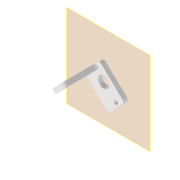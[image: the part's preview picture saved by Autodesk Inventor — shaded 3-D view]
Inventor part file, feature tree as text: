
AUTODESK INVENTOR PART (.ipt)
format: ipt  version: 2022 (Build 260153000, 153)  size: 141,824 bytes
history: native  units: mm
features: reference x11, extrude x3, sketch x3, other x3, plane x2, fillet x1, projected_geometry x1
ambient origin geometry x8: Origin, YZ Plane, XZ Plane, XY Plane, X Axis, Y Axis, Z Axis, Center Point
bodies: Body1 (feature_tree)
feature tree (24):
  plane  "Arbeitsebene3"
  extrude  "Extrusion4"  Depth=16.0mm
  sketch  "Skizze5"  dims[d17=24.0mm d18=3.0mm d19=0.0mm]
  plane  "Arbeitsebene4"
  extrude  "Extrusion5"  Depth=3.0mm TaperAngle=0.0deg
  extrude  "Extrusion6"  Depth=3.0mm TaperAngle=0.0deg
  fillet  "Rundung1"  Radius=10.0mm
  sketch  "Skizze4"  dims[d15=0.0mm d16=16.0mm]
  reference  "Referenz7"
  reference  "Referenz8"
  reference  "Referenz9"
  reference  "Referenz10"
  reference  "Referenz11"
  reference  "Referenz12"
  reference  "Referenz13"
  reference  "Referenz14"
  reference  "Referenz15"
  projected_geometry  "Projizierte Kontur1"
  sketch  "Skizze6"  dims[d20=3.0mm d21=3.0mm d22=0.0mm d23=10.0mm d24=0.0mm d25=2.0mm]
  reference  "Referenz16"
  reference  "Referenz17"
  other  "Baugruppe1"
  other  "IM_Matchboxscope_base_old:1"
  other  "00_Microlinearmotor:1"
